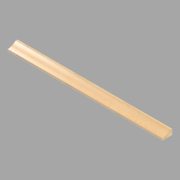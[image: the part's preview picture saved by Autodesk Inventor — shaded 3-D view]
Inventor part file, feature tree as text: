
AUTODESK INVENTOR PART (.ipt)
format: ipt  version: 2022.2 (Build 262287010, 287A)  size: 131,584 bytes
history: native  units: in
note: dims shown in document units (in); Inventor stores cm internally (conversion verified against a paired STEP export)
features: revolve x2, direct_edit x1
ambient origin geometry x8: Origin, YZ Plane, XZ Plane, XY Plane, X Axis, Y Axis, Z Axis, Center Point
bodies: Solid1 (feature_tree), Body1 (feature_tree)
feature tree (3):
  direct_edit  "Direct Edit1"
  revolve  "Rotate1"  [1 undecoded]
  revolve  "Rotate2"  [1 undecoded]
note: 2 required parameter values undecoded (feature->parameter linkage not recoverable at this tier; creation-order binding heuristic only, values carry confidence <= 0.55)
